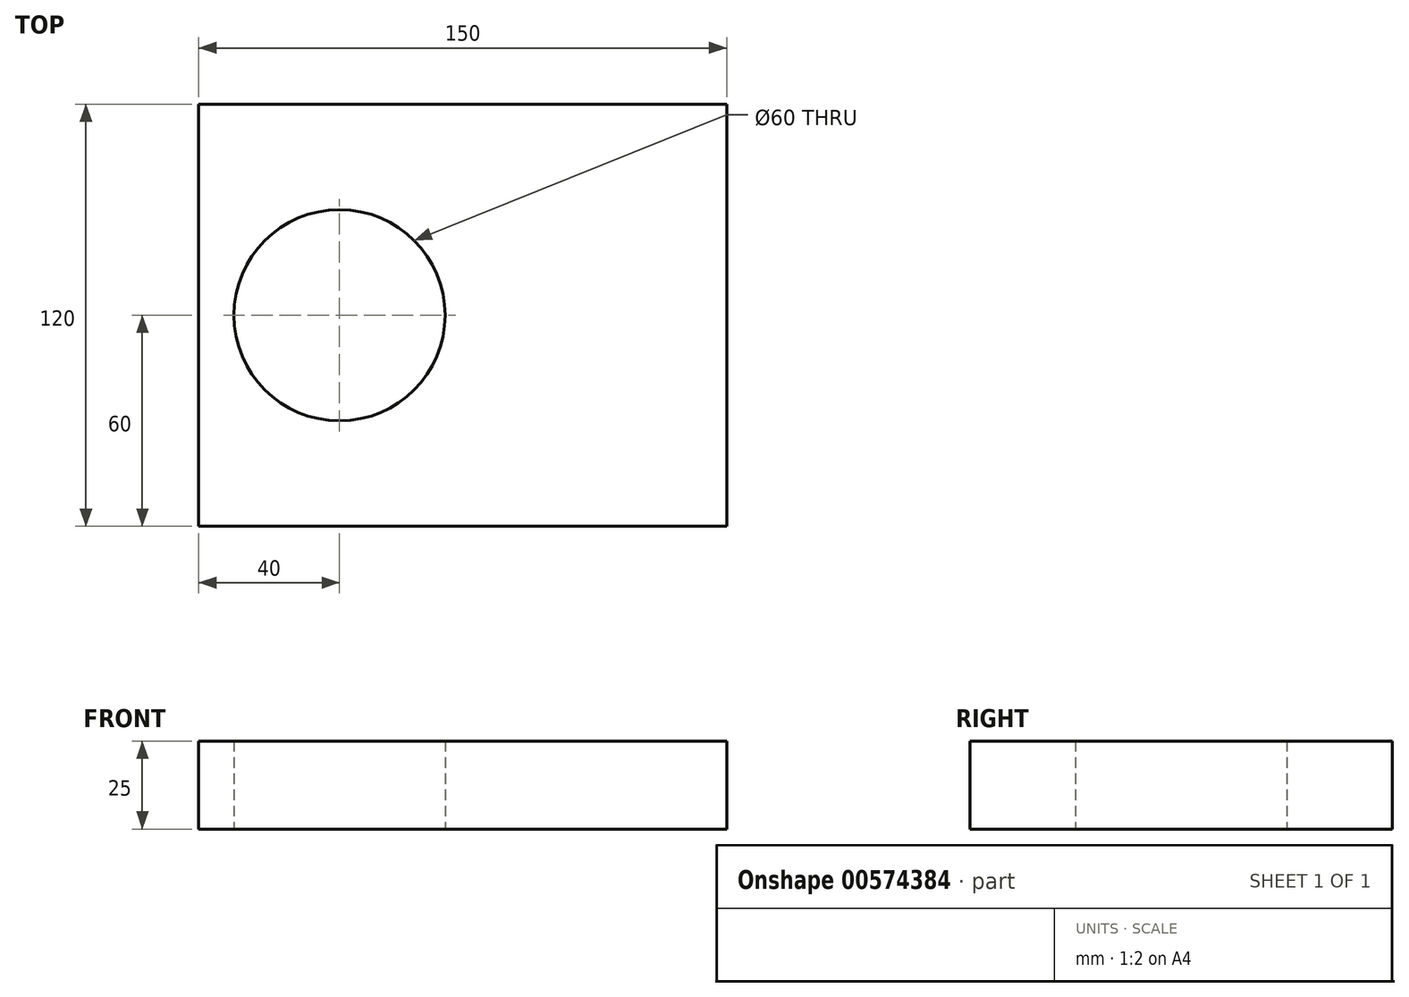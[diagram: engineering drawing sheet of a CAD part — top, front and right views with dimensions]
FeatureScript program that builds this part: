
annotation { "Feature Type Name" : "Feature", "Feature Type Description" : "" }
export const myFeature = defineFeature(function(context is Context, id is Id, definition is map)
    precondition{}
    {
        {
            var Q0;
            Q0=qCreatedBy(makeId("Top.planeOp"),FACE);
            var sketch = newSketch(context, id + "F0", { "sketchPlane" : qUnion([Q0])});
            skLineSegment(sketch, "E0.bottom", {"start": v(-50, 60) * mm, "end": v(100, 60) * mm});
            skLineSegment(sketch, "E0.top", {"start": v(-50, -60) * mm, "end": v(100, -60) * mm});
            skLineSegment(sketch, "E0.left", {"start": v(-50, 60) * mm, "end": v(-50, -60) * mm});
            skLineSegment(sketch, "E0.right", {"start": v(100, 60) * mm, "end": v(100, -60) * mm});
            skCircle(sketch, "E1", {"center": v(-10, 0) * mm, "radius": 30 * mm});
            skSolve(sketch);
        }
        {
            var Q0;
            Q0=makeQuery(id+"F0.imprint","IMPRINT",FACE,{"disambiguationData":[TD([[makeQuery(id+"F0.imprint","IMPRINT",EDGE,{"derivedFrom":sQuery(id+"F0.wireOp",EDGE,"E0.bottom")}),-1.0]])]});
            extrude(context, id + "F1", {"entities" : qUnion([Q0]), "depth" : 25 * mm, "offsetDistance" : 25 * mm});
        }
    });
